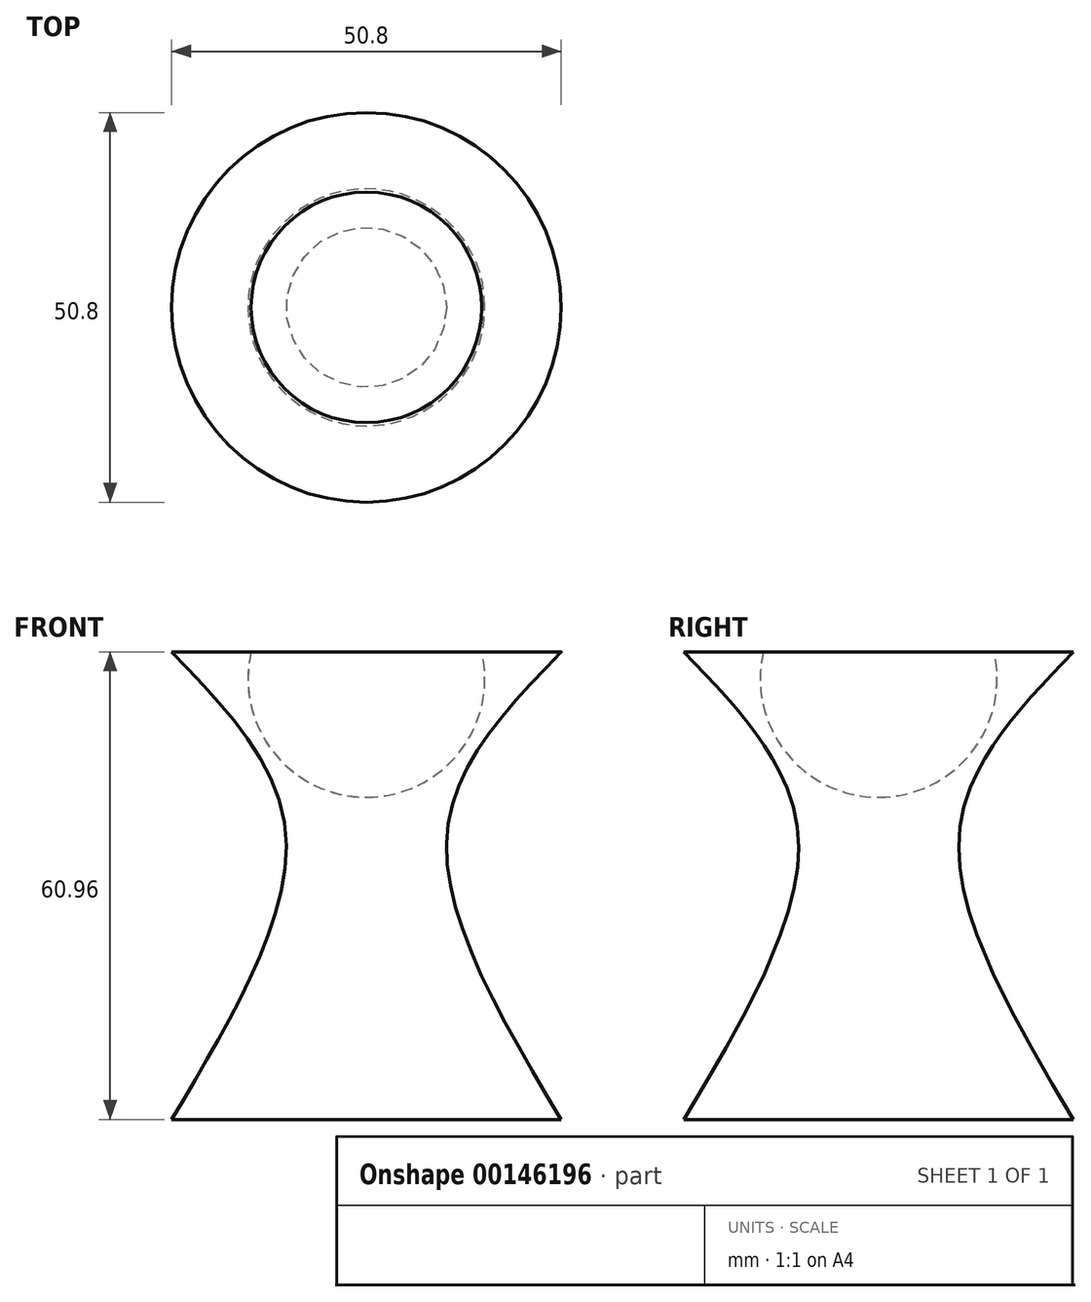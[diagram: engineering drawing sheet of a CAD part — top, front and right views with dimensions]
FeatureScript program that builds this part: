
annotation { "Feature Type Name" : "Feature", "Feature Type Description" : "" }
export const myFeature = defineFeature(function(context is Context, id is Id, definition is map)
    precondition{}
    {
        {
            var Q0;
            Q0=qCreatedBy(makeId("Top.planeOp"),FACE);
            var sketch = newSketch(context, id + "F0", { "sketchPlane" : qUnion([Q0])});
            skCircle(sketch, "E0", {"center": v(0, 0) * mm, "radius": 25.4 * mm});
            skSolve(sketch);
        }
        {
            var Q0;
            Q0 = qSketchRegion(id + "F0", true);
            extrude(context, id + "F1", {"entities" : qUnion([Q0]), "depth" : 60.96 * mm});
        }
        {
            var Q0;
            Q0=qCreatedBy(makeId("Front.planeOp"),FACE);
            var sketch = newSketch(context, id + "F2", { "sketchPlane" : qUnion([Q0])});
            skLineSegment(sketch, "E1", {"start": v(-25.4, 72.62) * mm, "end": v(-25.4, -15.5) * mm, "construction": true});
            skLineSegment(sketch, "E2", {"start": v(0, 68.04) * mm, "end": v(0, -17.54) * mm, "construction": true});
            skLineSegment(sketch, "E3", {"start": v(-41.69, 60.92) * mm, "end": v(38.98, 60.92) * mm, "construction": true});
            skFitSpline(sketch, "E4", {"points": [v(-25.4, 60.92) * mm, v(-10.52, 37.42) * mm, v(-25.4, 0) * mm], "startDerivative": vector(46.4, -47.99) * mm, "endDerivative": vector(-43.64, -73.09) * mm});
            skLineSegment(sketch, "E5", {"start": v(-25.4, 60.92) * mm, "end": v(-25.4, 0) * mm});
            skSolve(sketch);
        }
        {
            var Q0;
            Q0 = qSketchRegion(id + "F2", true);
            var Q1;
            Q1=sQuery(id+"F2.wireOp",EDGE,"E2");
            revolve(context, id + "F3", {"operationType" : NewBodyOperationType.REMOVE, "entities" : qUnion([Q0]), "axis" : qUnion([Q1]), "revolveType" : RevolveType.FULL});
        }
        {
            var Q0;
            Q0=qCreatedBy(makeId("Front.planeOp"),FACE);
            var sketch = newSketch(context, id + "F4", { "sketchPlane" : qUnion([Q0])});
            skArc(sketch, "E6", {"start": v(0, 42) * mm, "mid": v(15.44, 57.44) * mm, "end": v(0, 72.88) * mm});
            skLineSegment(sketch, "E7", {"start": v(0, 72.88) * mm, "end": v(0, 42) * mm});
            skSolve(sketch);
        }
        {
            var Q0;
            Q0=makeQuery(id+"F4.imprint","IMPRINT",FACE,{"disambiguationData":[TD([[makeQuery(id+"F4.imprint","IMPRINT",EDGE,{"derivedFrom":sQuery(id+"F4.wireOp",EDGE,"E6")}),1.0]])]});
            var Q1;
            Q1=sQuery(id+"F4.wireOp",EDGE,"E7");
            revolve(context, id + "F5", {"operationType" : NewBodyOperationType.REMOVE, "entities" : qUnion([Q0]), "axis" : qUnion([Q1]), "revolveType" : RevolveType.FULL, "oppositeDirection" : true});
        }
    });
